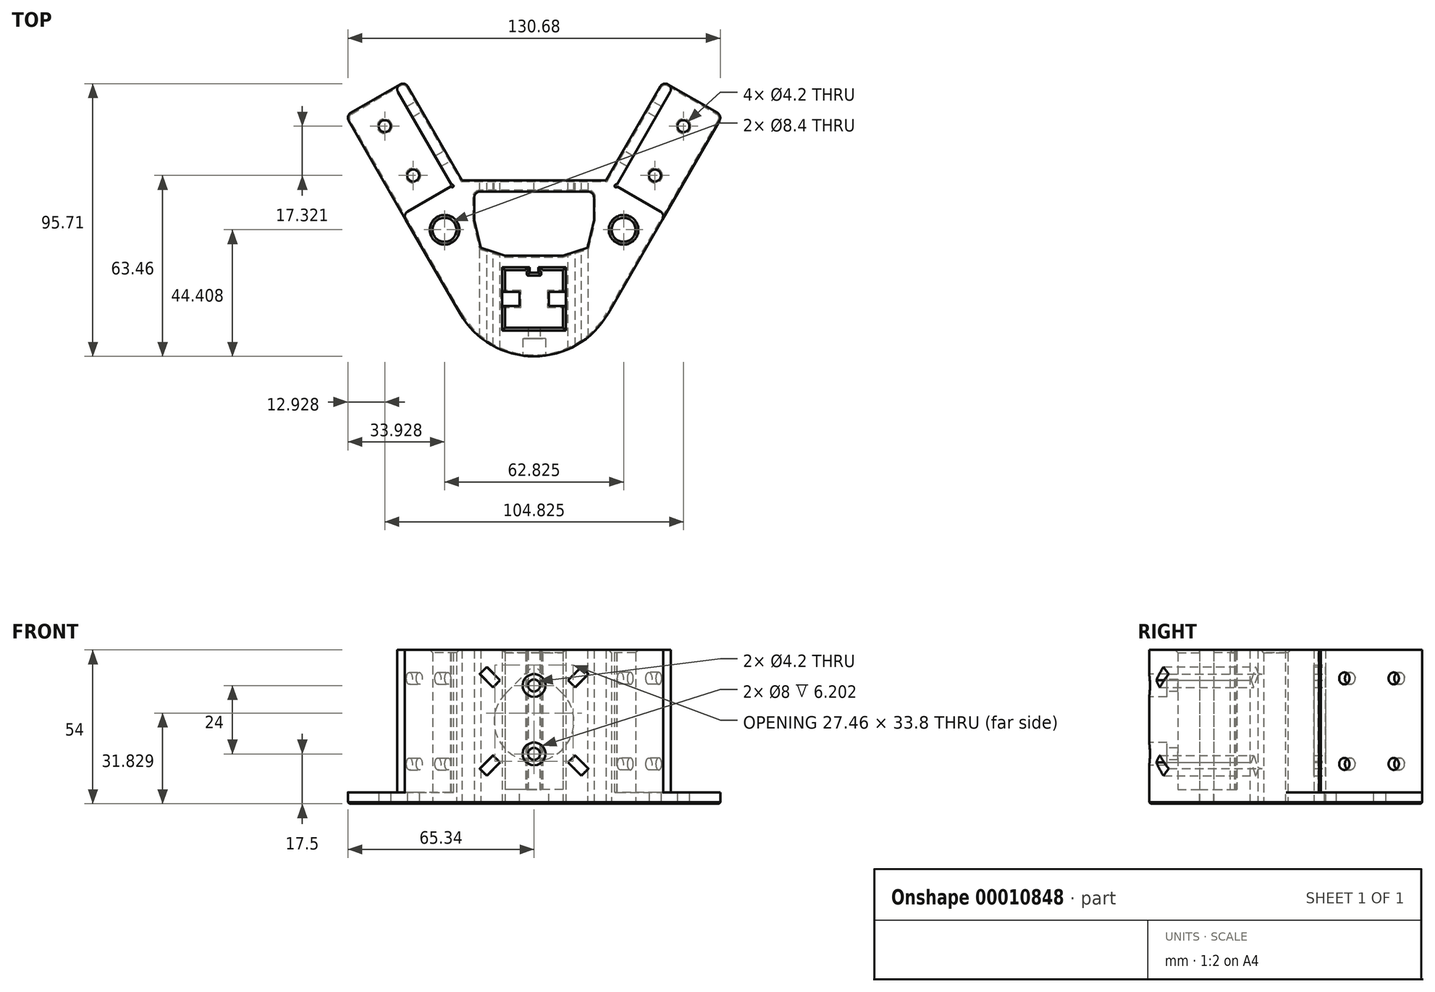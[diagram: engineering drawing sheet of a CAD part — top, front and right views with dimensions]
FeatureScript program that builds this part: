
annotation { "Feature Type Name" : "Feature", "Feature Type Description" : "" }
export const myFeature = defineFeature(function(context is Context, id is Id, definition is map)
    precondition{}
    {
        {
            var Q0;
            Q0=qCreatedBy(makeId("Top.planeOp"),FACE);
            var sketch = newSketch(context, id + "F0", { "sketchPlane" : qUnion([Q0])});
            skLineSegment(sketch, "E0.rect.bottom", {"start": v(10.15, -10.15) * mm, "end": v(-10.15, -10.15) * mm});
            skLineSegment(sketch, "E0.rect.top", {"start": v(10.15, 10.15) * mm, "end": v(-10.15, 10.15) * mm});
            skLineSegment(sketch, "E0.rect.left", {"start": v(10.15, -10.15) * mm, "end": v(10.15, 10.15) * mm});
            skLineSegment(sketch, "E0.rect.right", {"start": v(-10.15, -10.15) * mm, "end": v(-10.15, 10.15) * mm});
            skPoint(sketch, "E0.rect.middle", {"position": v(0, 0) * mm});
            skLineSegment(sketch, "E1", {"start": v(-10.15, -2.5) * mm, "end": v(-8.15, -2.5) * mm});
            skLineSegment(sketch, "E2", {"start": v(-8.15, -2.5) * mm, "end": v(-8.15, 2.5) * mm});
            skLineSegment(sketch, "E3", {"start": v(-8.15, 2.5) * mm, "end": v(-10.15, 2.5) * mm});
            skLineSegment(sketch, "E4", {"start": v(-2.5, 10.15) * mm, "end": v(-2.5, 8.15) * mm});
            skLineSegment(sketch, "E5", {"start": v(-2.5, 8.15) * mm, "end": v(2.5, 8.15) * mm});
            skLineSegment(sketch, "E6", {"start": v(2.5, 8.15) * mm, "end": v(2.5, 10.15) * mm});
            skLineSegment(sketch, "E7", {"start": v(10.15, 2.5) * mm, "end": v(8.15, 2.5) * mm});
            skLineSegment(sketch, "E8", {"start": v(8.15, 2.5) * mm, "end": v(8.15, -2.5) * mm});
            skLineSegment(sketch, "E9", {"start": v(8.15, -2.5) * mm, "end": v(10.15, -2.5) * mm});
            skLineSegment(sketch, "E10", {"start": v(-25.98, -5.15) * mm, "end": v(-66.07, 64.3) * mm});
            skLineSegment(sketch, "E11", {"start": v(-66.07, 64.3) * mm, "end": v(-45.29, 76.3) * mm});
            skLineSegment(sketch, "E12", {"start": v(-45.29, 76.3) * mm, "end": v(-25.29, 41.65) * mm});
            skLineSegment(sketch, "E13", {"start": v(-25.29, 41.65) * mm, "end": v(25.29, 41.65) * mm});
            skLineSegment(sketch, "E14", {"start": v(25.29, 41.65) * mm, "end": v(45.29, 76.3) * mm});
            skLineSegment(sketch, "E15", {"start": v(45.29, 76.3) * mm, "end": v(66.07, 64.3) * mm});
            skLineSegment(sketch, "E16", {"start": v(66.07, 64.3) * mm, "end": v(25.98, -5.15) * mm});
            skPoint(sketch, "E17.visualSharp", {"position": v(0, -50.15) * mm});
            skArc(sketch, "E17.filletArc", {"start": v(-25.98, -5.15) * mm, "mid": v(0, -20.15) * mm, "end": v(25.98, -5.15) * mm});
            skLineSegment(sketch, "E18", {"start": v(-48.75, 74.3) * mm, "end": v(-28.75, 39.65) * mm});
            skLineSegment(sketch, "E19", {"start": v(-28.75, 39.65) * mm, "end": v(-46.07, 29.65) * mm});
            skLineSegment(sketch, "E20", {"start": v(48.75, 74.3) * mm, "end": v(28.75, 39.65) * mm});
            skLineSegment(sketch, "E21", {"start": v(28.75, 39.65) * mm, "end": v(46.07, 29.65) * mm});
            skLineSegment(sketch, "E22", {"start": v(-28.75, 39.65) * mm, "end": v(-25.29, 41.65) * mm, "construction": true});
            skLineSegment(sketch, "E23", {"start": v(-57.41, 69.3) * mm, "end": v(-37.41, 34.65) * mm, "construction": true});
            skCircle(sketch, "E24", {"center": v(-52.41, 60.63) * mm, "radius": 2.1 * mm});
            skCircle(sketch, "E25", {"center": v(-42.41, 43.31) * mm, "radius": 2.1 * mm});
            skCircle(sketch, "E26", {"center": v(52.41, 60.63) * mm, "radius": 2.1 * mm});
            skCircle(sketch, "E27", {"center": v(42.41, 43.31) * mm, "radius": 2.1 * mm});
            skLineSegment(sketch, "E28", {"start": v(-21, 37.65) * mm, "end": v(21, 37.65) * mm});
            skLineSegment(sketch, "E29", {"start": v(21, 37.65) * mm, "end": v(21, 27.65) * mm});
            skLineSegment(sketch, "E30", {"start": v(10.15, 15.15) * mm, "end": v(-10.15, 15.15) * mm});
            skLineSegment(sketch, "E31", {"start": v(-21, 27.65) * mm, "end": v(-21, 37.65) * mm});
            skLineSegment(sketch, "E32", {"start": v(-21, 27.65) * mm, "end": v(-18.71, 17.91) * mm});
            skLineSegment(sketch, "E33", {"start": v(-18.71, 17.91) * mm, "end": v(-10.15, 15.15) * mm});
            skLineSegment(sketch, "E34", {"start": v(21, 27.65) * mm, "end": v(18.71, 17.91) * mm});
            skLineSegment(sketch, "E35", {"start": v(18.71, 17.91) * mm, "end": v(10.15, 15.15) * mm});
            skLineSegment(sketch, "E36", {"start": v(-37.41, 34.65) * mm, "end": v(-20.62, 5.56) * mm, "construction": true});
            skCircle(sketch, "E37", {"center": v(-31.41, 24.26) * mm, "radius": 4.2 * mm});
            skLineSegment(sketch, "E38", {"start": v(0, -71.13) * mm, "end": v(0, 233.1) * mm, "construction": true});
            skCircle(sketch, "E39", {"center": v(31.41, 24.26) * mm, "radius": 4.2 * mm});
            skSolve(sketch);
        }
        {
            var Q0;
            {var subQ5=sQuery(id+"F0.wireOp",EDGE,"E0.rect.bottom");Q0=makeQuery(id+"F0.imprint","IMPRINT",FACE,{"disambiguationData":[TD([[makeQuery(id+"F0.imprint","IMPRINT",EDGE,{"derivedFrom":subQ5}),1.0]])]});}
            var Q1;
            {var subQ1=sQuery(id+"F0.wireOp",EDGE,"E18");Q1=makeQuery(id+"F0.imprint","IMPRINT",FACE,{"disambiguationData":[TD([[makeQuery(id+"F0.imprint","IMPRINT",EDGE,{"derivedFrom":subQ1}),-1.0]])]});}
            var Q2;
            {var subQ0=sQuery(id+"F0.wireOp",EDGE,"E20");Q2=makeQuery(id+"F0.imprint","IMPRINT",FACE,{"disambiguationData":[TD([[makeQuery(id+"F0.imprint","IMPRINT",EDGE,{"derivedFrom":subQ0}),1.0]])]});}
            var Q3;
            {var subQ1=sQuery(id+"F0.wireOp",EDGE,"E1");Q3=makeQuery(id+"F0.imprint","IMPRINT",FACE,{"disambiguationData":[TD([[makeQuery(id+"F0.imprint","IMPRINT",EDGE,{"derivedFrom":subQ1}),1.0]])]});}
            var Q4;
            {var subQ1=sQuery(id+"F0.wireOp",EDGE,"E4");Q4=makeQuery(id+"F0.imprint","IMPRINT",FACE,{"disambiguationData":[TD([[makeQuery(id+"F0.imprint","IMPRINT",EDGE,{"derivedFrom":subQ1}),1.0]])]});}
            var Q5;
            {var subQ1=sQuery(id+"F0.wireOp",EDGE,"E7");Q5=makeQuery(id+"F0.imprint","IMPRINT",FACE,{"disambiguationData":[TD([[makeQuery(id+"F0.imprint","IMPRINT",EDGE,{"derivedFrom":subQ1}),1.0]])]});}
            extrude(context, id + "F1", {"entities" : qUnion([Q0, Q1, Q2, Q3, Q4, Q5]), "depth" : 4 * mm});
        }
        {
            var Q0;
            Q0=makeQuery(id+"F1.opExtrude","CAP_FACE",FACE,{"disambiguationData":[OSD([sQuery(id+"F0.wireOp",EDGE,"E0.rect.bottom"),sQuery(id+"F0.wireOp",EDGE,"E0.rect.top"),sQuery(id+"F0.wireOp",EDGE,"E0.rect.left"),sQuery(id+"F0.wireOp",EDGE,"E0.rect.right"),sQuery(id+"F0.wireOp",EDGE,"E1"),sQuery(id+"F0.wireOp",EDGE,"E2"),sQuery(id+"F0.wireOp",EDGE,"E3"),sQuery(id+"F0.wireOp",EDGE,"E4"),sQuery(id+"F0.wireOp",EDGE,"E5"),sQuery(id+"F0.wireOp",EDGE,"E6"),sQuery(id+"F0.wireOp",EDGE,"E7"),sQuery(id+"F0.wireOp",EDGE,"E8"),sQuery(id+"F0.wireOp",EDGE,"E9"),sQuery(id+"F0.wireOp",EDGE,"E10"),sQuery(id+"F0.wireOp",EDGE,"E11"),sQuery(id+"F0.wireOp",EDGE,"E12"),sQuery(id+"F0.wireOp",EDGE,"E13"),sQuery(id+"F0.wireOp",EDGE,"E14"),sQuery(id+"F0.wireOp",EDGE,"E15"),sQuery(id+"F0.wireOp",EDGE,"E16"),sQuery(id+"F0.wireOp",EDGE,"E17.filletArc"),sQuery(id+"F0.wireOp",EDGE,"E24"),sQuery(id+"F0.wireOp",EDGE,"E25"),sQuery(id+"F0.wireOp",EDGE,"E26"),sQuery(id+"F0.wireOp",EDGE,"E27"),sQuery(id+"F0.wireOp",EDGE,"E28"),sQuery(id+"F0.wireOp",EDGE,"E29"),sQuery(id+"F0.wireOp",EDGE,"E30"),sQuery(id+"F0.wireOp",EDGE,"E31"),sQuery(id+"F0.wireOp",EDGE,"E32"),sQuery(id+"F0.wireOp",EDGE,"E33"),sQuery(id+"F0.wireOp",EDGE,"E34"),sQuery(id+"F0.wireOp",EDGE,"E35"),sQuery(id+"F0.wireOp",EDGE,"E37"),sQuery(id+"F0.wireOp",EDGE,"E39")])],"isStart":false});
            var sketch = newSketch(context, id + "F2", { "sketchPlane" : qUnion([Q0])});
            skLineSegment(sketch, "E40.0", {"start": v(-48.75, 74.3) * mm, "end": v(-28.75, 39.65) * mm});
            skLineSegment(sketch, "E41.0", {"start": v(-28.75, 39.65) * mm, "end": v(-46.07, 29.65) * mm});
            skLineSegment(sketch, "E42.0", {"start": v(48.75, 74.3) * mm, "end": v(28.75, 39.65) * mm});
            skLineSegment(sketch, "E43.0", {"start": v(28.75, 39.65) * mm, "end": v(46.07, 29.65) * mm});
            skSolve(sketch);
        }
        {
            var Q0;
            {var subQ7=sQuery(id+"F2.wireOp",EDGE,"E40.0");Q0=makeQuery(id+"F2.imprint","IMPRINT",FACE,{"disambiguationData":[TD([[makeQuery(id+"F2.imprint","IMPRINT",EDGE,{"derivedFrom":subQ7}),1.0]])]});}
            extrude(context, id + "F3", {"entities" : qUnion([Q0]), "operationType" : NewBodyOperationType.ADD, "depth" : 50 * mm});
        }
        {
            var Q0;
            {var subQ0=sQuery(id+"F0.wireOp",EDGE,"E13");Q0=makeQuery(id+"F3.boolean.opBoolean","MERGE",FACE,{"derivedFrom":[makeQuery(id+"F1.opExtrude","SWEPT_FACE",FACE,{"disambiguationData":[OSD([subQ0])]}),makeQuery(id+"F3.opExtrude","SWEPT_FACE",FACE,{"disambiguationData":[OSD([subQ0])]})]});}
            var sketch = newSketch(context, id + "F4", { "sketchPlane" : qUnion([Q0])});
            skCircle(sketch, "E44", {"center": v(0, 28.93) * mm, "radius": 14 * mm});
            skLineSegment(sketch, "E45", {"start": v(0, 28.93) * mm, "end": v(-14.76, 43.7) * mm, "construction": true});
            skLineSegment(sketch, "E46", {"start": v(-19.07, 45.53) * mm, "end": v(-16.6, 48) * mm});
            skLineSegment(sketch, "E47", {"start": v(-16.6, 48) * mm, "end": v(-11.93, 43.33) * mm});
            skLineSegment(sketch, "E48", {"start": v(-11.93, 43.33) * mm, "end": v(-14.4, 40.86) * mm});
            skLineSegment(sketch, "E49", {"start": v(-14.4, 40.86) * mm, "end": v(-19.07, 45.53) * mm});
            skLineSegment(sketch, "E50.1.0", {"start": v(-11.93, 14.53) * mm, "end": v(-16.6, 9.86) * mm});
            skLineSegment(sketch, "E50.1.1", {"start": v(-16.6, 9.86) * mm, "end": v(-19.07, 12.33) * mm});
            skLineSegment(sketch, "E50.1.2", {"start": v(-19.07, 12.33) * mm, "end": v(-14.4, 17) * mm});
            skLineSegment(sketch, "E50.1.3", {"start": v(-14.4, 17) * mm, "end": v(-11.93, 14.53) * mm});
            skLineSegment(sketch, "E50.2.0", {"start": v(14.4, 17) * mm, "end": v(19.07, 12.33) * mm});
            skLineSegment(sketch, "E50.2.1", {"start": v(19.07, 12.33) * mm, "end": v(16.6, 9.86) * mm});
            skLineSegment(sketch, "E50.2.2", {"start": v(16.6, 9.86) * mm, "end": v(11.93, 14.53) * mm});
            skLineSegment(sketch, "E50.2.3", {"start": v(11.93, 14.53) * mm, "end": v(14.4, 17) * mm});
            skLineSegment(sketch, "E50.3.0", {"start": v(11.93, 43.33) * mm, "end": v(16.6, 48) * mm});
            skLineSegment(sketch, "E50.3.1", {"start": v(16.6, 48) * mm, "end": v(19.07, 45.53) * mm});
            skLineSegment(sketch, "E50.3.2", {"start": v(19.07, 45.53) * mm, "end": v(14.4, 40.86) * mm});
            skLineSegment(sketch, "E50.3.3", {"start": v(14.4, 40.86) * mm, "end": v(11.93, 43.33) * mm});
            skLineSegment(sketch, "E51", {"start": v(0, 48.73) * mm, "end": v(-9.9, 38.83) * mm});
            skLineSegment(sketch, "E52", {"start": v(0, 48.73) * mm, "end": v(9.9, 38.83) * mm});
            skSolve(sketch);
        }
        {
            var Q0;
            Q0=makeQuery(id+"F4.imprint","IMPRINT",FACE,{"disambiguationData":[TD([[makeQuery(id+"F4.imprint","IMPRINT",EDGE,{"derivedFrom":sQuery(id+"F4.wireOp",EDGE,"E44")}),1.0]])]});
            var Q1;
            {var subQ1=sQuery(id+"F4.wireOp",EDGE,"E51");Q1=makeQuery(id+"F4.imprint","IMPRINT",FACE,{"disambiguationData":[TD([[makeQuery(id+"F4.imprint","IMPRINT",EDGE,{"derivedFrom":subQ1}),1.0]])]});}
            extrude(context, id + "F5", {"entities" : qUnion([Q0, Q1]), "operationType" : NewBodyOperationType.REMOVE, "endBound" : BoundingType.UP_TO_NEXT, "oppositeDirection" : true, "depth" : 25 * mm});
        }
        {
            var Q0;
            Q0=makeQuery(id+"F4.imprint","IMPRINT",FACE,{"disambiguationData":[TD([[makeQuery(id+"F4.imprint","IMPRINT",EDGE,{"derivedFrom":sQuery(id+"F4.wireOp",EDGE,"E46")}),-1.0]])]});
            var Q1;
            Q1=makeQuery(id+"F4.imprint","IMPRINT",FACE,{"disambiguationData":[TD([[makeQuery(id+"F4.imprint","IMPRINT",EDGE,{"derivedFrom":sQuery(id+"F4.wireOp",EDGE,"E50.3.0")}),-1.0]])]});
            var Q2;
            Q2=makeQuery(id+"F4.imprint","IMPRINT",FACE,{"disambiguationData":[TD([[makeQuery(id+"F4.imprint","IMPRINT",EDGE,{"derivedFrom":sQuery(id+"F4.wireOp",EDGE,"E50.2.0")}),-1.0]])]});
            var Q3;
            Q3=makeQuery(id+"F4.imprint","IMPRINT",FACE,{"disambiguationData":[TD([[makeQuery(id+"F4.imprint","IMPRINT",EDGE,{"derivedFrom":sQuery(id+"F4.wireOp",EDGE,"E50.1.0")}),-1.0]])]});
            extrude(context, id + "F6", {"entities" : qUnion([Q0, Q1, Q2, Q3]), "operationType" : NewBodyOperationType.REMOVE, "endBound" : BoundingType.THROUGH_ALL, "oppositeDirection" : true, "depth" : 25 * mm});
        }
        {
            var Q0;
            {var subQ11=sQuery(id+"F0.wireOp",EDGE,"E0.rect.bottom");Q0=makeQuery(id+"F0.imprint","IMPRINT",FACE,{"disambiguationData":[TD([[makeQuery(id+"F0.imprint","IMPRINT",EDGE,{"derivedFrom":subQ11}),-1.0]])]});}
            extrude(context, id + "F7", {"entities" : qUnion([Q0]), "operationType" : NewBodyOperationType.ADD, "depth" : 5 * mm});
        }
        {
            var Q0;
            {var subQ0=sQuery(id+"F0.wireOp",EDGE,"E28");Q0=makeQuery(id+"F3.boolean.opBoolean","MERGE",FACE,{"derivedFrom":[makeQuery(id+"F1.opExtrude","SWEPT_FACE",FACE,{"disambiguationData":[OSD([subQ0])]}),makeQuery(id+"F3.opExtrude","SWEPT_FACE",FACE,{"disambiguationData":[OSD([subQ0])]})]});}
            cPlane(context, id + "F8", {"entities" : qUnion([Q0]), "cplaneType" : CPlaneType.OFFSET, "offset" : 100 * mm, "width" : 150 * mm, "height" : 150 * mm});
        }
        {
            var Q0;
            Q0=qCreatedBy(id+"F8.planeOp",FACE);
            var sketch = newSketch(context, id + "F9", { "sketchPlane" : qUnion([Q0])});
            skCircle(sketch, "E53", {"center": v(0, 41.5) * mm, "radius": 2.1 * mm});
            skCircle(sketch, "E54", {"center": v(0, 41.5) * mm, "radius": 4 * mm});
            skCircle(sketch, "E55", {"center": v(0, 17.5) * mm, "radius": 2.1 * mm});
            skCircle(sketch, "E56", {"center": v(0, 17.5) * mm, "radius": 4 * mm});
            skSolve(sketch);
        }
        {
            var Q0;
            Q0=makeQuery(id+"F9.imprint","IMPRINT",FACE,{"disambiguationData":[TD([[makeQuery(id+"F9.imprint","IMPRINT",EDGE,{"derivedFrom":sQuery(id+"F9.wireOp",EDGE,"E53")}),1.0]])]});
            var Q1;
            Q1=makeQuery(id+"F9.imprint","IMPRINT",FACE,{"disambiguationData":[TD([[makeQuery(id+"F9.imprint","IMPRINT",EDGE,{"derivedFrom":sQuery(id+"F9.wireOp",EDGE,"E55")}),1.0]])]});
            var Q2;
            {var subQ0=sQuery(id+"F0.wireOp",EDGE,"E0.rect.bottom");Q2=makeQuery(id+"F3.boolean.opBoolean","MERGE",FACE,{"derivedFrom":[makeQuery(id+"F1.opExtrude","SWEPT_FACE",FACE,{"disambiguationData":[OSD([subQ0])]}),makeQuery(id+"F3.opExtrude","SWEPT_FACE",FACE,{"disambiguationData":[OSD([subQ0])]})]});}
            extrude(context, id + "F10", {"entities" : qUnion([Q0, Q1]), "operationType" : NewBodyOperationType.REMOVE, "endBound" : BoundingType.UP_TO_SURFACE, "oppositeDirection" : true, "endBoundEntityFace" : qUnion([Q2]), "depth" : 25 * mm});
        }
        {
            var Q0;
            Q0=makeQuery(id+"F9.imprint","IMPRINT",FACE,{"disambiguationData":[TD([[makeQuery(id+"F9.imprint","IMPRINT",EDGE,{"derivedFrom":sQuery(id+"F9.wireOp",EDGE,"E53")}),-1.0]])]});
            var Q1;
            Q1=makeQuery(id+"F9.imprint","IMPRINT",FACE,{"disambiguationData":[TD([[makeQuery(id+"F9.imprint","IMPRINT",EDGE,{"derivedFrom":sQuery(id+"F9.wireOp",EDGE,"E55")}),-1.0]])]});
            extrude(context, id + "F11", {"entities" : qUnion([Q0, Q1]), "operationType" : NewBodyOperationType.REMOVE, "oppositeDirection" : true, "depth" : 48.4 * mm});
        }
        {
            var Q0;
            {var subQ0=sQuery(id+"F0.wireOp",EDGE,"E12");Q0=makeQuery(id+"F3.boolean.opBoolean","MERGE",FACE,{"derivedFrom":[makeQuery(id+"F1.opExtrude","SWEPT_FACE",FACE,{"disambiguationData":[OSD([subQ0])]}),makeQuery(id+"F3.opExtrude","SWEPT_FACE",FACE,{"disambiguationData":[OSD([subQ0])]})]});}
            var sketch = newSketch(context, id + "F12", { "sketchPlane" : qUnion([Q0])});
            skCircle(sketch, "E57", {"center": v(78.71, 44) * mm, "radius": 2.1 * mm});
            skCircle(sketch, "E58", {"center": v(58.71, 44) * mm, "radius": 2.1 * mm});
            skCircle(sketch, "E59", {"center": v(78.71, 14) * mm, "radius": 2.1 * mm});
            skCircle(sketch, "E60", {"center": v(58.71, 14) * mm, "radius": 2.1 * mm});
            skSolve(sketch);
        }
        {
            var Q0;
            Q0 = qSketchRegion(id + "F12", true);
            extrude(context, id + "F13", {"entities" : qUnion([Q0]), "operationType" : NewBodyOperationType.REMOVE, "oppositeDirection" : true, "depth" : 25 * mm});
        }
        {
            var Q0;
            {var subQ0=sQuery(id+"F0.wireOp",EDGE,"E14");Q0=makeQuery(id+"F3.boolean.opBoolean","MERGE",FACE,{"derivedFrom":[makeQuery(id+"F1.opExtrude","SWEPT_FACE",FACE,{"disambiguationData":[OSD([subQ0])]}),makeQuery(id+"F3.opExtrude","SWEPT_FACE",FACE,{"disambiguationData":[OSD([subQ0])]})]});}
            var sketch = newSketch(context, id + "F14", { "sketchPlane" : qUnion([Q0])});
            skCircle(sketch, "E61", {"center": v(-78.71, 44) * mm, "radius": 2.1 * mm});
            skCircle(sketch, "E62", {"center": v(-58.71, 44) * mm, "radius": 2.1 * mm});
            skCircle(sketch, "E63", {"center": v(-78.71, 14) * mm, "radius": 2.1 * mm});
            skCircle(sketch, "E64", {"center": v(-58.71, 14) * mm, "radius": 2.1 * mm});
            skSolve(sketch);
        }
        {
            var Q0;
            Q0 = qSketchRegion(id + "F14", true);
            extrude(context, id + "F15", {"entities" : qUnion([Q0]), "operationType" : NewBodyOperationType.REMOVE, "oppositeDirection" : true, "depth" : 25 * mm});
        }
        {
            var Q0;
            Q0=makeQuery(id+"F3.opExtrude","CAP_EDGE",EDGE,{"disambiguationData":[OSD([sQuery(id+"F0.wireOp",EDGE,"E0.rect.bottom")])],"isStart":false});
            var Q1;
            {var subQ0=sQuery(id+"F0.wireOp",EDGE,"E0.rect.left");Q1=makeQuery(id+"F3.opExtrude","CAP_EDGE",EDGE,{"disambiguationData":[OSD([subQ0]),TDD([makeQuery(id+"F2.imprint","IMPRINT",EDGE,{"derivedFrom":makeQuery(id+"F1.opExtrude","CAP_EDGE",EDGE,{"disambiguationData":[OSD([subQ0]),TDD([makeQuery(id+"F0.imprint","IMPRINT",EDGE,{"disambiguationData":[TD([[makeQuery(id+"F0.imprint","INTERSECT",VERTEX,{"derivedFrom":[sQuery(id+"F0.wireOp",EDGE,"E0.rect.bottom"),subQ0]}),-1.0]])],"derivedFrom":subQ0})])],"isStart":false})})])],"isStart":false});}
            var Q2;
            Q2=makeQuery(id+"F3.opExtrude","CAP_EDGE",EDGE,{"disambiguationData":[OSD([sQuery(id+"F0.wireOp",EDGE,"E9")])],"isStart":false});
            var Q3;
            Q3=makeQuery(id+"F3.opExtrude","CAP_EDGE",EDGE,{"disambiguationData":[OSD([sQuery(id+"F0.wireOp",EDGE,"E8")])],"isStart":false});
            var Q4;
            Q4=makeQuery(id+"F3.opExtrude","CAP_EDGE",EDGE,{"disambiguationData":[OSD([sQuery(id+"F0.wireOp",EDGE,"E7")])],"isStart":false});
            var Q5;
            {var subQ0=sQuery(id+"F0.wireOp",EDGE,"E0.rect.left");Q5=makeQuery(id+"F3.opExtrude","CAP_EDGE",EDGE,{"disambiguationData":[OSD([subQ0]),TDD([makeQuery(id+"F2.imprint","IMPRINT",EDGE,{"derivedFrom":makeQuery(id+"F1.opExtrude","CAP_EDGE",EDGE,{"disambiguationData":[OSD([subQ0]),TDD([makeQuery(id+"F0.imprint","IMPRINT",EDGE,{"disambiguationData":[TD([[makeQuery(id+"F0.imprint","INTERSECT",VERTEX,{"derivedFrom":[sQuery(id+"F0.wireOp",EDGE,"E0.rect.top"),subQ0]}),1.0]])],"derivedFrom":subQ0})])],"isStart":false})})])],"isStart":false});}
            var Q6;
            {var subQ0=sQuery(id+"F0.wireOp",EDGE,"E0.rect.top");Q6=makeQuery(id+"F3.opExtrude","CAP_EDGE",EDGE,{"disambiguationData":[OSD([subQ0]),TDD([makeQuery(id+"F2.imprint","IMPRINT",EDGE,{"derivedFrom":makeQuery(id+"F1.opExtrude","CAP_EDGE",EDGE,{"disambiguationData":[OSD([subQ0]),TDD([makeQuery(id+"F0.imprint","IMPRINT",EDGE,{"disambiguationData":[TD([[makeQuery(id+"F0.imprint","INTERSECT",VERTEX,{"derivedFrom":[subQ0,sQuery(id+"F0.wireOp",EDGE,"E0.rect.left")]}),-1.0]])],"derivedFrom":subQ0})])],"isStart":false})})])],"isStart":false});}
            var Q7;
            Q7=makeQuery(id+"F3.opExtrude","CAP_EDGE",EDGE,{"disambiguationData":[OSD([sQuery(id+"F0.wireOp",EDGE,"E6")])],"isStart":false});
            var Q8;
            Q8=makeQuery(id+"F3.opExtrude","CAP_EDGE",EDGE,{"disambiguationData":[OSD([sQuery(id+"F0.wireOp",EDGE,"E5")])],"isStart":false});
            var Q9;
            Q9=makeQuery(id+"F3.opExtrude","CAP_EDGE",EDGE,{"disambiguationData":[OSD([sQuery(id+"F0.wireOp",EDGE,"E4")])],"isStart":false});
            var Q10;
            {var subQ0=sQuery(id+"F0.wireOp",EDGE,"E0.rect.top");Q10=makeQuery(id+"F3.opExtrude","CAP_EDGE",EDGE,{"disambiguationData":[OSD([subQ0]),TDD([makeQuery(id+"F2.imprint","IMPRINT",EDGE,{"derivedFrom":makeQuery(id+"F1.opExtrude","CAP_EDGE",EDGE,{"disambiguationData":[OSD([subQ0]),TDD([makeQuery(id+"F0.imprint","IMPRINT",EDGE,{"disambiguationData":[TD([[makeQuery(id+"F0.imprint","INTERSECT",VERTEX,{"derivedFrom":[subQ0,sQuery(id+"F0.wireOp",EDGE,"E0.rect.right")]}),1.0]])],"derivedFrom":subQ0})])],"isStart":false})})])],"isStart":false});}
            var Q11;
            {var subQ0=sQuery(id+"F0.wireOp",EDGE,"E0.rect.right");Q11=makeQuery(id+"F3.opExtrude","CAP_EDGE",EDGE,{"disambiguationData":[OSD([subQ0]),TDD([makeQuery(id+"F2.imprint","IMPRINT",EDGE,{"derivedFrom":makeQuery(id+"F1.opExtrude","CAP_EDGE",EDGE,{"disambiguationData":[OSD([subQ0]),TDD([makeQuery(id+"F0.imprint","IMPRINT",EDGE,{"disambiguationData":[TD([[makeQuery(id+"F0.imprint","INTERSECT",VERTEX,{"derivedFrom":[sQuery(id+"F0.wireOp",EDGE,"E0.rect.top"),subQ0]}),1.0]])],"derivedFrom":subQ0})])],"isStart":false})})])],"isStart":false});}
            var Q12;
            Q12=makeQuery(id+"F3.opExtrude","CAP_EDGE",EDGE,{"disambiguationData":[OSD([sQuery(id+"F0.wireOp",EDGE,"E3")])],"isStart":false});
            var Q13;
            Q13=makeQuery(id+"F3.opExtrude","CAP_EDGE",EDGE,{"disambiguationData":[OSD([sQuery(id+"F0.wireOp",EDGE,"E2")])],"isStart":false});
            var Q14;
            Q14=makeQuery(id+"F3.opExtrude","CAP_EDGE",EDGE,{"disambiguationData":[OSD([sQuery(id+"F0.wireOp",EDGE,"E1")])],"isStart":false});
            var Q15;
            {var subQ0=sQuery(id+"F0.wireOp",EDGE,"E0.rect.right");Q15=makeQuery(id+"F3.opExtrude","CAP_EDGE",EDGE,{"disambiguationData":[OSD([subQ0]),TDD([makeQuery(id+"F2.imprint","IMPRINT",EDGE,{"derivedFrom":makeQuery(id+"F1.opExtrude","CAP_EDGE",EDGE,{"disambiguationData":[OSD([subQ0]),TDD([makeQuery(id+"F0.imprint","IMPRINT",EDGE,{"disambiguationData":[TD([[makeQuery(id+"F0.imprint","INTERSECT",VERTEX,{"derivedFrom":[sQuery(id+"F0.wireOp",EDGE,"E0.rect.bottom"),subQ0]}),-1.0]])],"derivedFrom":subQ0})])],"isStart":false})})])],"isStart":false});}
            var Q16;
            Q16=makeQuery(id+"F3.opExtrude","CAP_EDGE",EDGE,{"disambiguationData":[OSD([sQuery(id+"F0.wireOp",EDGE,"E39")])],"isStart":false});
            var Q17;
            Q17=makeQuery(id+"F3.opExtrude","CAP_EDGE",EDGE,{"disambiguationData":[OSD([sQuery(id+"F0.wireOp",EDGE,"E37")])],"isStart":false});
            chamfer(context, id + "F16", {"entities" : qUnion([Q0, Q1, Q2, Q3, Q4, Q5, Q6, Q7, Q8, Q9, Q10, Q11, Q12, Q13, Q14, Q15, Q16, Q17]), "width" : 1 * mm, "tangentPropagation" : true});
        }
        {
            var Q0;
            Q0=makeQuery(id+"F3.opExtrude","CAP_FACE",FACE,{"disambiguationData":[OSD([sQuery(id+"F0.wireOp",EDGE,"E0.rect.bottom"),sQuery(id+"F0.wireOp",EDGE,"E0.rect.top"),sQuery(id+"F0.wireOp",EDGE,"E0.rect.left"),sQuery(id+"F0.wireOp",EDGE,"E0.rect.right"),sQuery(id+"F0.wireOp",EDGE,"E1"),sQuery(id+"F0.wireOp",EDGE,"E2"),sQuery(id+"F0.wireOp",EDGE,"E3"),sQuery(id+"F0.wireOp",EDGE,"E4"),sQuery(id+"F0.wireOp",EDGE,"E5"),sQuery(id+"F0.wireOp",EDGE,"E6"),sQuery(id+"F0.wireOp",EDGE,"E7"),sQuery(id+"F0.wireOp",EDGE,"E8"),sQuery(id+"F0.wireOp",EDGE,"E9"),sQuery(id+"F0.wireOp",EDGE,"E10"),sQuery(id+"F0.wireOp",EDGE,"E11"),sQuery(id+"F0.wireOp",EDGE,"E12"),sQuery(id+"F0.wireOp",EDGE,"E13"),sQuery(id+"F0.wireOp",EDGE,"E14"),sQuery(id+"F0.wireOp",EDGE,"E15"),sQuery(id+"F0.wireOp",EDGE,"E16"),sQuery(id+"F0.wireOp",EDGE,"E17.filletArc"),sQuery(id+"F0.wireOp",EDGE,"E28"),sQuery(id+"F0.wireOp",EDGE,"E29"),sQuery(id+"F0.wireOp",EDGE,"E30"),sQuery(id+"F0.wireOp",EDGE,"E31"),sQuery(id+"F0.wireOp",EDGE,"E32"),sQuery(id+"F0.wireOp",EDGE,"E33"),sQuery(id+"F0.wireOp",EDGE,"E34"),sQuery(id+"F0.wireOp",EDGE,"E35"),sQuery(id+"F0.wireOp",EDGE,"E37"),sQuery(id+"F0.wireOp",EDGE,"E39"),sQuery(id+"F2.wireOp",EDGE,"E40.0"),sQuery(id+"F2.wireOp",EDGE,"E41.0"),sQuery(id+"F2.wireOp",EDGE,"E42.0"),sQuery(id+"F2.wireOp",EDGE,"E43.0")])],"isStart":false});
            var sketch = newSketch(context, id + "F17", { "sketchPlane" : qUnion([Q0])});
            skCircle(sketch, "E65", {"center": v(-28.75, 39.65) * mm, "radius": 0.5 * mm});
            skCircle(sketch, "E66", {"center": v(28.75, 39.65) * mm, "radius": 0.5 * mm});
            skSolve(sketch);
        }
        {
            var Q0;
            {var subQ1=sQuery(id+"F17.wireOp",EDGE,"E65");var subQ3=makeQuery(id+"F3.opExtrude","CAP_EDGE",EDGE,{"disambiguationData":[OSD([sQuery(id+"F2.wireOp",EDGE,"E40.0")])],"isStart":false});var subQ5=makeQuery(id+"F17.imprint","INTERSECT",VERTEX,{"derivedFrom":[subQ3,subQ1]});Q0=makeQuery(id+"F17.imprint","IMPRINT",FACE,{"disambiguationData":[TD([[makeQuery(id+"F17.imprint","IMPRINT",EDGE,{"disambiguationData":[TD([[subQ5,1.0]])],"derivedFrom":subQ1}),1.0]])]});}
            var Q1;
            {var subQ1=sQuery(id+"F17.wireOp",EDGE,"E66");var subQ3=makeQuery(id+"F3.opExtrude","CAP_EDGE",EDGE,{"disambiguationData":[OSD([sQuery(id+"F2.wireOp",EDGE,"E42.0")])],"isStart":false});var subQ5=makeQuery(id+"F17.imprint","INTERSECT",VERTEX,{"derivedFrom":[subQ3,subQ1]});Q1=makeQuery(id+"F17.imprint","IMPRINT",FACE,{"disambiguationData":[TD([[makeQuery(id+"F17.imprint","IMPRINT",EDGE,{"disambiguationData":[TD([[subQ5,-1.0]])],"derivedFrom":subQ1}),1.0]])]});}
            var Q2;
            {var subQ0=sQuery(id+"F0.wireOp",EDGE,"E10");var subQ1=sQuery(id+"F0.wireOp",EDGE,"E11");var subQ2=sQuery(id+"F0.wireOp",EDGE,"E24");var subQ3=sQuery(id+"F0.wireOp",EDGE,"E25");Q2=makeQuery(id+"F3.boolean.opBoolean","SPLIT",FACE,{"disambiguationData":[TD([makeQuery(id+"F1.opExtrude","SWEPT_FACE",FACE,{"disambiguationData":[OSD([subQ0])]})])],"derivedFrom":makeQuery(id+"F1.opExtrude","CAP_FACE",FACE,{"disambiguationData":[OSD([sQuery(id+"F0.wireOp",EDGE,"E0.rect.bottom"),sQuery(id+"F0.wireOp",EDGE,"E0.rect.top"),sQuery(id+"F0.wireOp",EDGE,"E0.rect.left"),sQuery(id+"F0.wireOp",EDGE,"E0.rect.right"),sQuery(id+"F0.wireOp",EDGE,"E1"),sQuery(id+"F0.wireOp",EDGE,"E2"),sQuery(id+"F0.wireOp",EDGE,"E3"),sQuery(id+"F0.wireOp",EDGE,"E4"),sQuery(id+"F0.wireOp",EDGE,"E5"),sQuery(id+"F0.wireOp",EDGE,"E6"),sQuery(id+"F0.wireOp",EDGE,"E7"),sQuery(id+"F0.wireOp",EDGE,"E8"),sQuery(id+"F0.wireOp",EDGE,"E9"),subQ0,subQ1,sQuery(id+"F0.wireOp",EDGE,"E12"),sQuery(id+"F0.wireOp",EDGE,"E13"),sQuery(id+"F0.wireOp",EDGE,"E14"),sQuery(id+"F0.wireOp",EDGE,"E15"),sQuery(id+"F0.wireOp",EDGE,"E16"),sQuery(id+"F0.wireOp",EDGE,"E17.filletArc"),subQ2,subQ3,sQuery(id+"F0.wireOp",EDGE,"E26"),sQuery(id+"F0.wireOp",EDGE,"E27"),sQuery(id+"F0.wireOp",EDGE,"E28"),sQuery(id+"F0.wireOp",EDGE,"E29"),sQuery(id+"F0.wireOp",EDGE,"E30"),sQuery(id+"F0.wireOp",EDGE,"E31"),sQuery(id+"F0.wireOp",EDGE,"E32"),sQuery(id+"F0.wireOp",EDGE,"E33"),sQuery(id+"F0.wireOp",EDGE,"E34"),sQuery(id+"F0.wireOp",EDGE,"E35"),sQuery(id+"F0.wireOp",EDGE,"E37"),sQuery(id+"F0.wireOp",EDGE,"E39")])],"isStart":false})});}
            extrude(context, id + "F18", {"entities" : qUnion([Q0, Q1]), "operationType" : NewBodyOperationType.REMOVE, "endBound" : BoundingType.UP_TO_SURFACE, "oppositeDirection" : true, "endBoundEntityFace" : qUnion([Q2]), "depth" : 25 * mm});
        }
        {
            var Q0;
            Q0=makeQuery(id+"F18.boolean.opBoolean","COPY",EDGE,{"derivedFrom":makeQuery(id+"F18.opExtrude","SWEPT_EDGE",EDGE,{"disambiguationData":[OSD([sQuery(id+"F2.wireOp",EDGE,"E40.0"),sQuery(id+"F17.wireOp",EDGE,"E65")])]})});
            var Q1;
            Q1=makeQuery(id+"F18.boolean.opBoolean","COPY",EDGE,{"derivedFrom":makeQuery(id+"F18.opExtrude","SWEPT_EDGE",EDGE,{"disambiguationData":[OSD([sQuery(id+"F2.wireOp",EDGE,"E41.0"),sQuery(id+"F17.wireOp",EDGE,"E65")])]})});
            var Q2;
            Q2=makeQuery(id+"F18.boolean.opBoolean","COPY",EDGE,{"derivedFrom":makeQuery(id+"F18.opExtrude","SWEPT_EDGE",EDGE,{"disambiguationData":[OSD([sQuery(id+"F2.wireOp",EDGE,"E42.0"),sQuery(id+"F17.wireOp",EDGE,"E66")])]})});
            var Q3;
            Q3=makeQuery(id+"F18.boolean.opBoolean","COPY",EDGE,{"derivedFrom":makeQuery(id+"F18.opExtrude","SWEPT_EDGE",EDGE,{"disambiguationData":[OSD([sQuery(id+"F2.wireOp",EDGE,"E43.0"),sQuery(id+"F17.wireOp",EDGE,"E66")])]})});
            var Q4;
            Q4=makeQuery(id+"F3.opExtrude","SWEPT_EDGE",EDGE,{"disambiguationData":[OSD([sQuery(id+"F0.wireOp",EDGE,"E10"),sQuery(id+"F2.wireOp",EDGE,"E41.0")])]});
            var Q5;
            Q5=makeQuery(id+"F1.opExtrude","SWEPT_EDGE",EDGE,{"disambiguationData":[OSD([sQuery(id+"F0.wireOp",EDGE,"E10"),sQuery(id+"F0.wireOp",EDGE,"E11")])]});
            var Q6;
            Q6=makeQuery(id+"F3.opExtrude","SWEPT_EDGE",EDGE,{"disambiguationData":[OSD([sQuery(id+"F0.wireOp",EDGE,"E11"),sQuery(id+"F2.wireOp",EDGE,"E40.0")])]});
            var Q7;
            {var subQ0=sQuery(id+"F0.wireOp",EDGE,"E11");var subQ1=sQuery(id+"F0.wireOp",EDGE,"E12");Q7=makeQuery(id+"F3.boolean.opBoolean","MERGE",EDGE,{"derivedFrom":[makeQuery(id+"F1.opExtrude","SWEPT_EDGE",EDGE,{"disambiguationData":[OSD([subQ0,subQ1])]}),makeQuery(id+"F3.opExtrude","SWEPT_EDGE",EDGE,{"disambiguationData":[OSD([subQ0,subQ1])]})]});}
            var Q8;
            {var subQ0=sQuery(id+"F0.wireOp",EDGE,"E14");var subQ1=sQuery(id+"F0.wireOp",EDGE,"E15");Q8=makeQuery(id+"F3.boolean.opBoolean","MERGE",EDGE,{"derivedFrom":[makeQuery(id+"F1.opExtrude","SWEPT_EDGE",EDGE,{"disambiguationData":[OSD([subQ0,subQ1])]}),makeQuery(id+"F3.opExtrude","SWEPT_EDGE",EDGE,{"disambiguationData":[OSD([subQ0,subQ1])]})]});}
            var Q9;
            Q9=makeQuery(id+"F3.opExtrude","SWEPT_EDGE",EDGE,{"disambiguationData":[OSD([sQuery(id+"F0.wireOp",EDGE,"E15"),sQuery(id+"F2.wireOp",EDGE,"E42.0")])]});
            var Q10;
            Q10=makeQuery(id+"F1.opExtrude","SWEPT_EDGE",EDGE,{"disambiguationData":[OSD([sQuery(id+"F0.wireOp",EDGE,"E15"),sQuery(id+"F0.wireOp",EDGE,"E16")])]});
            var Q11;
            Q11=makeQuery(id+"F3.opExtrude","SWEPT_EDGE",EDGE,{"disambiguationData":[OSD([sQuery(id+"F0.wireOp",EDGE,"E16"),sQuery(id+"F2.wireOp",EDGE,"E43.0")])]});
            var Q12;
            {var subQ0=sQuery(id+"F0.wireOp",EDGE,"E28");var subQ1=sQuery(id+"F0.wireOp",EDGE,"E31");Q12=makeQuery(id+"F3.boolean.opBoolean","MERGE",EDGE,{"derivedFrom":[makeQuery(id+"F1.opExtrude","SWEPT_EDGE",EDGE,{"disambiguationData":[OSD([subQ0,subQ1])]}),makeQuery(id+"F3.opExtrude","SWEPT_EDGE",EDGE,{"disambiguationData":[OSD([subQ0,subQ1])]})]});}
            var Q13;
            {var subQ0=sQuery(id+"F0.wireOp",EDGE,"E28");var subQ1=sQuery(id+"F0.wireOp",EDGE,"E29");Q13=makeQuery(id+"F3.boolean.opBoolean","MERGE",EDGE,{"derivedFrom":[makeQuery(id+"F1.opExtrude","SWEPT_EDGE",EDGE,{"disambiguationData":[OSD([subQ0,subQ1])]}),makeQuery(id+"F3.opExtrude","SWEPT_EDGE",EDGE,{"disambiguationData":[OSD([subQ0,subQ1])]})]});}
            fillet(context, id + "F19", {"entities" : qUnion([Q0, Q1, Q2, Q3, Q4, Q5, Q6, Q7, Q8, Q9, Q10, Q11, Q12, Q13]), "radius" : 2 * mm, "tangentPropagation" : true, "allowEdgeOverflow" : false});
        }
        {
            var Q0;
            {var subQ0=sQuery(id+"F0.wireOp",EDGE,"E0.rect.bottom");var subQ1=sQuery(id+"F0.wireOp",EDGE,"E0.rect.top");var subQ2=sQuery(id+"F0.wireOp",EDGE,"E0.rect.left");var subQ3=sQuery(id+"F0.wireOp",EDGE,"E0.rect.right");var subQ4=sQuery(id+"F0.wireOp",EDGE,"E1");var subQ5=sQuery(id+"F0.wireOp",EDGE,"E2");var subQ6=sQuery(id+"F0.wireOp",EDGE,"E3");var subQ7=sQuery(id+"F0.wireOp",EDGE,"E4");var subQ8=sQuery(id+"F0.wireOp",EDGE,"E5");var subQ9=sQuery(id+"F0.wireOp",EDGE,"E6");var subQ10=sQuery(id+"F0.wireOp",EDGE,"E7");var subQ11=sQuery(id+"F0.wireOp",EDGE,"E8");var subQ12=sQuery(id+"F0.wireOp",EDGE,"E9");Q0=makeQuery(id+"F7.boolean.opBoolean","MERGE",FACE,{"derivedFrom":[makeQuery(id+"F1.opExtrude","CAP_FACE",FACE,{"disambiguationData":[OSD([subQ0,subQ1,subQ2,subQ3,subQ4,subQ5,subQ6,subQ7,subQ8,subQ9,subQ10,subQ11,subQ12,sQuery(id+"F0.wireOp",EDGE,"E10"),sQuery(id+"F0.wireOp",EDGE,"E11"),sQuery(id+"F0.wireOp",EDGE,"E12"),sQuery(id+"F0.wireOp",EDGE,"E13"),sQuery(id+"F0.wireOp",EDGE,"E14"),sQuery(id+"F0.wireOp",EDGE,"E15"),sQuery(id+"F0.wireOp",EDGE,"E16"),sQuery(id+"F0.wireOp",EDGE,"E17.filletArc"),sQuery(id+"F0.wireOp",EDGE,"E24"),sQuery(id+"F0.wireOp",EDGE,"E25"),sQuery(id+"F0.wireOp",EDGE,"E26"),sQuery(id+"F0.wireOp",EDGE,"E27"),sQuery(id+"F0.wireOp",EDGE,"E28"),sQuery(id+"F0.wireOp",EDGE,"E29"),sQuery(id+"F0.wireOp",EDGE,"E30"),sQuery(id+"F0.wireOp",EDGE,"E31"),sQuery(id+"F0.wireOp",EDGE,"E32"),sQuery(id+"F0.wireOp",EDGE,"E33"),sQuery(id+"F0.wireOp",EDGE,"E34"),sQuery(id+"F0.wireOp",EDGE,"E35"),sQuery(id+"F0.wireOp",EDGE,"E37"),sQuery(id+"F0.wireOp",EDGE,"E39")])],"isStart":true}),makeQuery(id+"F7.opExtrude","CAP_FACE",FACE,{"disambiguationData":[OSD([subQ0,subQ1,subQ2,subQ3,subQ4,subQ5,subQ6,subQ7,subQ8,subQ9,subQ10,subQ11,subQ12])],"isStart":true})]});}
            chamfer(context, id + "F20", {"entities" : qUnion([Q0]), "width" : 0.5 * mm, "tangentPropagation" : true});
        }
        {
            var Q0;
            Q0=makeQuery(id+"F7.opExtrude","CAP_FACE",FACE,{"disambiguationData":[OSD([sQuery(id+"F0.wireOp",EDGE,"E0.rect.bottom"),sQuery(id+"F0.wireOp",EDGE,"E0.rect.top"),sQuery(id+"F0.wireOp",EDGE,"E0.rect.left"),sQuery(id+"F0.wireOp",EDGE,"E0.rect.right"),sQuery(id+"F0.wireOp",EDGE,"E1"),sQuery(id+"F0.wireOp",EDGE,"E2"),sQuery(id+"F0.wireOp",EDGE,"E3"),sQuery(id+"F0.wireOp",EDGE,"E4"),sQuery(id+"F0.wireOp",EDGE,"E5"),sQuery(id+"F0.wireOp",EDGE,"E6"),sQuery(id+"F0.wireOp",EDGE,"E7"),sQuery(id+"F0.wireOp",EDGE,"E8"),sQuery(id+"F0.wireOp",EDGE,"E9")])],"isStart":false});
            var sketch = newSketch(context, id + "F21", { "sketchPlane" : qUnion([Q0])});
            skCircle(sketch, "E67", {"center": v(2.5, 10.15) * mm, "radius": 0.5 * mm});
            skCircle(sketch, "E68", {"center": v(-2.5, 10.15) * mm, "radius": 0.5 * mm});
            skPoint(sketch, "E69.centerSnap0", {"position": v(8.15, 0) * mm});
            skLineSegment(sketch, "E70.bottom", {"start": v(-8.15, -2.5) * mm, "end": v(-11.15, -2.5) * mm});
            skLineSegment(sketch, "E70.top", {"start": v(-8.15, 2.5) * mm, "end": v(-11.15, 2.5) * mm});
            skLineSegment(sketch, "E70.left", {"start": v(-8.15, -2.5) * mm, "end": v(-8.15, 2.5) * mm});
            skLineSegment(sketch, "E70.right", {"start": v(-11.15, -2.5) * mm, "end": v(-11.15, 2.5) * mm});
            skLineSegment(sketch, "E71.bottom", {"start": v(8.15, -2.5) * mm, "end": v(11.15, -2.5) * mm});
            skLineSegment(sketch, "E71.top", {"start": v(8.15, 2.5) * mm, "end": v(11.15, 2.5) * mm});
            skLineSegment(sketch, "E71.left", {"start": v(8.15, -2.5) * mm, "end": v(8.15, 2.5) * mm});
            skLineSegment(sketch, "E71.right", {"start": v(11.15, -2.5) * mm, "end": v(11.15, 2.5) * mm});
            skLineSegment(sketch, "E72.bottom", {"start": v(-8.15, -2.5) * mm, "end": v(-5.15, -2.5) * mm});
            skLineSegment(sketch, "E72.top", {"start": v(-8.15, 2.5) * mm, "end": v(-5.15, 2.5) * mm});
            skLineSegment(sketch, "E72.right", {"start": v(-5.15, -2.5) * mm, "end": v(-5.15, 2.5) * mm});
            skLineSegment(sketch, "E73.bottom", {"start": v(8.15, -2.5) * mm, "end": v(5.15, -2.5) * mm});
            skLineSegment(sketch, "E73.top", {"start": v(8.15, 2.5) * mm, "end": v(5.15, 2.5) * mm});
            skLineSegment(sketch, "E73.right", {"start": v(5.15, -2.5) * mm, "end": v(5.15, 2.5) * mm});
            skSolve(sketch);
        }
        {
            var Q0;
            {var subQ0=sQuery(id+"F0.wireOp",EDGE,"E6");var subQ1=makeQuery(id+"F7.opExtrude","CAP_EDGE",EDGE,{"disambiguationData":[OSD([subQ0])],"isStart":false});var subQ2=sQuery(id+"F21.wireOp",EDGE,"E67");var subQ3=makeQuery(id+"F21.imprint","INTERSECT",VERTEX,{"derivedFrom":[subQ1,subQ2]});Q0=makeQuery(id+"F21.imprint","IMPRINT",FACE,{"disambiguationData":[TD([[makeQuery(id+"F21.imprint","IMPRINT",EDGE,{"disambiguationData":[TD([[subQ3,1.0]])],"derivedFrom":subQ2}),1.0]])]});}
            var Q1;
            {var subQ1=sQuery(id+"F0.wireOp",EDGE,"E4");var subQ3=sQuery(id+"F21.wireOp",EDGE,"E68");var subQ5=makeQuery(id+"F7.opExtrude","CAP_EDGE",EDGE,{"disambiguationData":[OSD([subQ1])],"isStart":false});var subQ7=makeQuery(id+"F21.imprint","INTERSECT",VERTEX,{"derivedFrom":[subQ5,subQ3]});Q1=makeQuery(id+"F21.imprint","IMPRINT",FACE,{"disambiguationData":[TD([[makeQuery(id+"F21.imprint","IMPRINT",EDGE,{"disambiguationData":[TD([[subQ7,-1.0]])],"derivedFrom":subQ3}),1.0]])]});}
            var Q2;
            {var subQ0=sQuery(id+"F21.wireOp",EDGE,"E71.top");var subQ1=sQuery(id+"F21.wireOp",EDGE,"33bc41b5-04d1-491b-9cc3-e2a9688a8de3");var subQ5=makeQuery(id+"F21.imprint","INTERSECT",VERTEX,{"disambiguationData":[OD(0.0)],"derivedFrom":[subQ1,subQ0]});Q2=makeQuery(id+"F21.imprint","IMPRINT",FACE,{"disambiguationData":[TD([[makeQuery(id+"F21.imprint","IMPRINT",EDGE,{"disambiguationData":[TD([[subQ5,1.0]])],"derivedFrom":subQ1}),1.0]])]});}
            var Q3;
            {var subQ1=sQuery(id+"F21.wireOp",EDGE,"E71.right");Q3=makeQuery(id+"F21.imprint","IMPRINT",FACE,{"disambiguationData":[TD([[makeQuery(id+"F21.imprint","IMPRINT",EDGE,{"derivedFrom":subQ1}),1.0]])]});}
            var Q4;
            {var subQ0=sQuery(id+"F21.wireOp",EDGE,"E70.top");var subQ1=sQuery(id+"F21.wireOp",EDGE,"531c82b6-ca83-49b7-b213-6d50da28229b");var subQ5=makeQuery(id+"F21.imprint","INTERSECT",VERTEX,{"disambiguationData":[OD(0.0)],"derivedFrom":[subQ1,subQ0]});Q4=makeQuery(id+"F21.imprint","IMPRINT",FACE,{"disambiguationData":[TD([[makeQuery(id+"F21.imprint","IMPRINT",EDGE,{"disambiguationData":[TD([[subQ5,-1.0]])],"derivedFrom":subQ1}),1.0]])]});}
            var Q5;
            {var subQ1=sQuery(id+"F21.wireOp",EDGE,"E70.right");Q5=makeQuery(id+"F21.imprint","IMPRINT",FACE,{"disambiguationData":[TD([[makeQuery(id+"F21.imprint","IMPRINT",EDGE,{"derivedFrom":subQ1}),-1.0]])]});}
            var Q6;
            Q6=makeQuery(id+"F3.opExtrude","CAP_FACE",FACE,{"disambiguationData":[OSD([sQuery(id+"F0.wireOp",EDGE,"E0.rect.bottom"),sQuery(id+"F0.wireOp",EDGE,"E0.rect.top"),sQuery(id+"F0.wireOp",EDGE,"E0.rect.left"),sQuery(id+"F0.wireOp",EDGE,"E0.rect.right"),sQuery(id+"F0.wireOp",EDGE,"E1"),sQuery(id+"F0.wireOp",EDGE,"E2"),sQuery(id+"F0.wireOp",EDGE,"E3"),sQuery(id+"F0.wireOp",EDGE,"E4"),sQuery(id+"F0.wireOp",EDGE,"E5"),sQuery(id+"F0.wireOp",EDGE,"E6"),sQuery(id+"F0.wireOp",EDGE,"E7"),sQuery(id+"F0.wireOp",EDGE,"E8"),sQuery(id+"F0.wireOp",EDGE,"E9"),sQuery(id+"F0.wireOp",EDGE,"E10"),sQuery(id+"F0.wireOp",EDGE,"E11"),sQuery(id+"F0.wireOp",EDGE,"E12"),sQuery(id+"F0.wireOp",EDGE,"E13"),sQuery(id+"F0.wireOp",EDGE,"E14"),sQuery(id+"F0.wireOp",EDGE,"E15"),sQuery(id+"F0.wireOp",EDGE,"E16"),sQuery(id+"F0.wireOp",EDGE,"E17.filletArc"),sQuery(id+"F0.wireOp",EDGE,"E28"),sQuery(id+"F0.wireOp",EDGE,"E29"),sQuery(id+"F0.wireOp",EDGE,"E30"),sQuery(id+"F0.wireOp",EDGE,"E31"),sQuery(id+"F0.wireOp",EDGE,"E32"),sQuery(id+"F0.wireOp",EDGE,"E33"),sQuery(id+"F0.wireOp",EDGE,"E34"),sQuery(id+"F0.wireOp",EDGE,"E35"),sQuery(id+"F0.wireOp",EDGE,"E37"),sQuery(id+"F0.wireOp",EDGE,"E39"),sQuery(id+"F2.wireOp",EDGE,"E40.0"),sQuery(id+"F2.wireOp",EDGE,"E41.0"),sQuery(id+"F2.wireOp",EDGE,"E42.0"),sQuery(id+"F2.wireOp",EDGE,"E43.0")])],"isStart":false});
            extrude(context, id + "F22", {"entities" : qUnion([Q0, Q1, Q2, Q3, Q4, Q5]), "operationType" : NewBodyOperationType.REMOVE, "endBound" : BoundingType.UP_TO_SURFACE, "endBoundEntityFace" : qUnion([Q6]), "depth" : 25 * mm});
        }
        {
            var Q0;
            {var subQ1=sQuery(id+"F21.wireOp",EDGE,"E70.right");Q0=makeQuery(id+"F21.imprint","IMPRINT",FACE,{"disambiguationData":[TD([[makeQuery(id+"F21.imprint","IMPRINT",EDGE,{"derivedFrom":subQ1}),-1.0]])]});}
            var Q1;
            {var subQ0=sQuery(id+"F21.wireOp",EDGE,"E70.top");var subQ1=sQuery(id+"F21.wireOp",EDGE,"531c82b6-ca83-49b7-b213-6d50da28229b");var subQ5=makeQuery(id+"F21.imprint","INTERSECT",VERTEX,{"disambiguationData":[OD(0.0)],"derivedFrom":[subQ1,subQ0]});Q1=makeQuery(id+"F21.imprint","IMPRINT",FACE,{"disambiguationData":[TD([[makeQuery(id+"F21.imprint","IMPRINT",EDGE,{"disambiguationData":[TD([[subQ5,-1.0]])],"derivedFrom":subQ1}),1.0]])]});}
            var Q2;
            {var subQ0=sQuery(id+"F21.wireOp",EDGE,"E70.bottom");var subQ1=sQuery(id+"F21.wireOp",EDGE,"ac99823a-828a-4d09-af91-54ec1811b827");var subQ2=makeQuery(id+"F21.imprint","INTERSECT",VERTEX,{"disambiguationData":[OD(0.0)],"derivedFrom":[subQ1,subQ0]});Q2=makeQuery(id+"F21.imprint","IMPRINT",FACE,{"disambiguationData":[TD([[makeQuery(id+"F21.imprint","IMPRINT",EDGE,{"disambiguationData":[TD([[subQ2,1.0]])],"derivedFrom":subQ1}),1.0]])]});}
            var Q3;
            Q3=makeQuery(id+"F21.imprint","IMPRINT",FACE,{"disambiguationData":[TD([[makeQuery(id+"F21.imprint","IMPRINT",EDGE,{"derivedFrom":sQuery(id+"F21.wireOp",EDGE,"E72.bottom")}),1.0]])]});
            var Q4;
            Q4=makeQuery(id+"F21.imprint","IMPRINT",FACE,{"disambiguationData":[TD([[makeQuery(id+"F21.imprint","IMPRINT",EDGE,{"derivedFrom":sQuery(id+"F21.wireOp",EDGE,"E73.bottom")}),-1.0]])]});
            var Q5;
            {var subQ1=sQuery(id+"F21.wireOp",EDGE,"E71.right");Q5=makeQuery(id+"F21.imprint","IMPRINT",FACE,{"disambiguationData":[TD([[makeQuery(id+"F21.imprint","IMPRINT",EDGE,{"derivedFrom":subQ1}),1.0]])]});}
            var Q6;
            {var subQ0=sQuery(id+"F21.wireOp",EDGE,"E71.top");var subQ1=sQuery(id+"F21.wireOp",EDGE,"33bc41b5-04d1-491b-9cc3-e2a9688a8de3");var subQ5=makeQuery(id+"F21.imprint","INTERSECT",VERTEX,{"disambiguationData":[OD(0.0)],"derivedFrom":[subQ1,subQ0]});Q6=makeQuery(id+"F21.imprint","IMPRINT",FACE,{"disambiguationData":[TD([[makeQuery(id+"F21.imprint","IMPRINT",EDGE,{"disambiguationData":[TD([[subQ5,1.0]])],"derivedFrom":subQ1}),1.0]])]});}
            var Q7;
            {var subQ0=sQuery(id+"F21.wireOp",EDGE,"E71.bottom");var subQ1=sQuery(id+"F21.wireOp",EDGE,"98ab61b8-06a1-4cc8-8eb2-811207c01617");var subQ5=makeQuery(id+"F21.imprint","INTERSECT",VERTEX,{"disambiguationData":[OD(0.0)],"derivedFrom":[subQ1,subQ0]});Q7=makeQuery(id+"F21.imprint","IMPRINT",FACE,{"disambiguationData":[TD([[makeQuery(id+"F21.imprint","IMPRINT",EDGE,{"disambiguationData":[TD([[subQ5,-1.0]])],"derivedFrom":subQ1}),1.0]])]});}
            extrude(context, id + "F23", {"entities" : qUnion([Q0, Q1, Q2, Q3, Q4, Q5, Q6, Q7]), "operationType" : NewBodyOperationType.REMOVE, "oppositeDirection" : true, "depth" : 25 * mm});
        }
        {
            var Q0;
            {var subQ0=sQuery(id+"F0.wireOp",EDGE,"E0.rect.bottom");var subQ1=sQuery(id+"F0.wireOp",EDGE,"E0.rect.top");var subQ2=sQuery(id+"F0.wireOp",EDGE,"E0.rect.left");var subQ3=sQuery(id+"F0.wireOp",EDGE,"E0.rect.right");var subQ4=sQuery(id+"F0.wireOp",EDGE,"E1");var subQ5=sQuery(id+"F0.wireOp",EDGE,"E2");var subQ6=sQuery(id+"F0.wireOp",EDGE,"E3");var subQ7=sQuery(id+"F0.wireOp",EDGE,"E4");var subQ8=sQuery(id+"F0.wireOp",EDGE,"E5");var subQ9=sQuery(id+"F0.wireOp",EDGE,"E6");var subQ10=sQuery(id+"F0.wireOp",EDGE,"E7");var subQ11=sQuery(id+"F0.wireOp",EDGE,"E8");var subQ12=sQuery(id+"F0.wireOp",EDGE,"E9");Q0=makeQuery(id+"F23.boolean.opBoolean","INTERSECT",EDGE,{"derivedFrom":[makeQuery(id+"F7.boolean.opBoolean","MERGE",FACE,{"derivedFrom":[makeQuery(id+"F1.opExtrude","CAP_FACE",FACE,{"disambiguationData":[OSD([subQ0,subQ1,subQ2,subQ3,subQ4,subQ5,subQ6,subQ7,subQ8,subQ9,subQ10,subQ11,subQ12,sQuery(id+"F0.wireOp",EDGE,"E10"),sQuery(id+"F0.wireOp",EDGE,"E11"),sQuery(id+"F0.wireOp",EDGE,"E12"),sQuery(id+"F0.wireOp",EDGE,"E13"),sQuery(id+"F0.wireOp",EDGE,"E14"),sQuery(id+"F0.wireOp",EDGE,"E15"),sQuery(id+"F0.wireOp",EDGE,"E16"),sQuery(id+"F0.wireOp",EDGE,"E17.filletArc"),sQuery(id+"F0.wireOp",EDGE,"E24"),sQuery(id+"F0.wireOp",EDGE,"E25"),sQuery(id+"F0.wireOp",EDGE,"E26"),sQuery(id+"F0.wireOp",EDGE,"E27"),sQuery(id+"F0.wireOp",EDGE,"E28"),sQuery(id+"F0.wireOp",EDGE,"E29"),sQuery(id+"F0.wireOp",EDGE,"E30"),sQuery(id+"F0.wireOp",EDGE,"E31"),sQuery(id+"F0.wireOp",EDGE,"E32"),sQuery(id+"F0.wireOp",EDGE,"E33"),sQuery(id+"F0.wireOp",EDGE,"E34"),sQuery(id+"F0.wireOp",EDGE,"E35"),sQuery(id+"F0.wireOp",EDGE,"E37"),sQuery(id+"F0.wireOp",EDGE,"E39")])],"isStart":true}),makeQuery(id+"F7.opExtrude","CAP_FACE",FACE,{"disambiguationData":[OSD([subQ0,subQ1,subQ2,subQ3,subQ4,subQ5,subQ6,subQ7,subQ8,subQ9,subQ10,subQ11,subQ12])],"isStart":true})]}),makeQuery(id+"F23.opExtrude","SWEPT_FACE",FACE,{"disambiguationData":[OSD([sQuery(id+"F21.wireOp",EDGE,"E70.right")])]})]});}
            var Q1;
            {var subQ0=sQuery(id+"F0.wireOp",EDGE,"E0.rect.bottom");var subQ1=sQuery(id+"F0.wireOp",EDGE,"E0.rect.top");var subQ2=sQuery(id+"F0.wireOp",EDGE,"E0.rect.left");var subQ3=sQuery(id+"F0.wireOp",EDGE,"E0.rect.right");var subQ4=sQuery(id+"F0.wireOp",EDGE,"E1");var subQ5=sQuery(id+"F0.wireOp",EDGE,"E2");var subQ6=sQuery(id+"F0.wireOp",EDGE,"E3");var subQ7=sQuery(id+"F0.wireOp",EDGE,"E4");var subQ8=sQuery(id+"F0.wireOp",EDGE,"E5");var subQ9=sQuery(id+"F0.wireOp",EDGE,"E6");var subQ10=sQuery(id+"F0.wireOp",EDGE,"E7");var subQ11=sQuery(id+"F0.wireOp",EDGE,"E8");var subQ12=sQuery(id+"F0.wireOp",EDGE,"E9");Q1=makeQuery(id+"F23.boolean.opBoolean","INTERSECT",EDGE,{"derivedFrom":[makeQuery(id+"F7.boolean.opBoolean","MERGE",FACE,{"derivedFrom":[makeQuery(id+"F1.opExtrude","CAP_FACE",FACE,{"disambiguationData":[OSD([subQ0,subQ1,subQ2,subQ3,subQ4,subQ5,subQ6,subQ7,subQ8,subQ9,subQ10,subQ11,subQ12,sQuery(id+"F0.wireOp",EDGE,"E10"),sQuery(id+"F0.wireOp",EDGE,"E11"),sQuery(id+"F0.wireOp",EDGE,"E12"),sQuery(id+"F0.wireOp",EDGE,"E13"),sQuery(id+"F0.wireOp",EDGE,"E14"),sQuery(id+"F0.wireOp",EDGE,"E15"),sQuery(id+"F0.wireOp",EDGE,"E16"),sQuery(id+"F0.wireOp",EDGE,"E17.filletArc"),sQuery(id+"F0.wireOp",EDGE,"E24"),sQuery(id+"F0.wireOp",EDGE,"E25"),sQuery(id+"F0.wireOp",EDGE,"E26"),sQuery(id+"F0.wireOp",EDGE,"E27"),sQuery(id+"F0.wireOp",EDGE,"E28"),sQuery(id+"F0.wireOp",EDGE,"E29"),sQuery(id+"F0.wireOp",EDGE,"E30"),sQuery(id+"F0.wireOp",EDGE,"E31"),sQuery(id+"F0.wireOp",EDGE,"E32"),sQuery(id+"F0.wireOp",EDGE,"E33"),sQuery(id+"F0.wireOp",EDGE,"E34"),sQuery(id+"F0.wireOp",EDGE,"E35"),sQuery(id+"F0.wireOp",EDGE,"E37"),sQuery(id+"F0.wireOp",EDGE,"E39")])],"isStart":true}),makeQuery(id+"F7.opExtrude","CAP_FACE",FACE,{"disambiguationData":[OSD([subQ0,subQ1,subQ2,subQ3,subQ4,subQ5,subQ6,subQ7,subQ8,subQ9,subQ10,subQ11,subQ12])],"isStart":true})]}),makeQuery(id+"F23.opExtrude","SWEPT_FACE",FACE,{"disambiguationData":[OSD([sQuery(id+"F21.wireOp",EDGE,"E70.bottom"),sQuery(id+"F21.wireOp",EDGE,"E72.bottom")])]})]});}
            var Q2;
            {var subQ0=sQuery(id+"F0.wireOp",EDGE,"E0.rect.bottom");var subQ1=sQuery(id+"F0.wireOp",EDGE,"E0.rect.top");var subQ2=sQuery(id+"F0.wireOp",EDGE,"E0.rect.left");var subQ3=sQuery(id+"F0.wireOp",EDGE,"E0.rect.right");var subQ4=sQuery(id+"F0.wireOp",EDGE,"E1");var subQ5=sQuery(id+"F0.wireOp",EDGE,"E2");var subQ6=sQuery(id+"F0.wireOp",EDGE,"E3");var subQ7=sQuery(id+"F0.wireOp",EDGE,"E4");var subQ8=sQuery(id+"F0.wireOp",EDGE,"E5");var subQ9=sQuery(id+"F0.wireOp",EDGE,"E6");var subQ10=sQuery(id+"F0.wireOp",EDGE,"E7");var subQ11=sQuery(id+"F0.wireOp",EDGE,"E8");var subQ12=sQuery(id+"F0.wireOp",EDGE,"E9");Q2=makeQuery(id+"F23.boolean.opBoolean","INTERSECT",EDGE,{"derivedFrom":[makeQuery(id+"F7.boolean.opBoolean","MERGE",FACE,{"derivedFrom":[makeQuery(id+"F1.opExtrude","CAP_FACE",FACE,{"disambiguationData":[OSD([subQ0,subQ1,subQ2,subQ3,subQ4,subQ5,subQ6,subQ7,subQ8,subQ9,subQ10,subQ11,subQ12,sQuery(id+"F0.wireOp",EDGE,"E10"),sQuery(id+"F0.wireOp",EDGE,"E11"),sQuery(id+"F0.wireOp",EDGE,"E12"),sQuery(id+"F0.wireOp",EDGE,"E13"),sQuery(id+"F0.wireOp",EDGE,"E14"),sQuery(id+"F0.wireOp",EDGE,"E15"),sQuery(id+"F0.wireOp",EDGE,"E16"),sQuery(id+"F0.wireOp",EDGE,"E17.filletArc"),sQuery(id+"F0.wireOp",EDGE,"E24"),sQuery(id+"F0.wireOp",EDGE,"E25"),sQuery(id+"F0.wireOp",EDGE,"E26"),sQuery(id+"F0.wireOp",EDGE,"E27"),sQuery(id+"F0.wireOp",EDGE,"E28"),sQuery(id+"F0.wireOp",EDGE,"E29"),sQuery(id+"F0.wireOp",EDGE,"E30"),sQuery(id+"F0.wireOp",EDGE,"E31"),sQuery(id+"F0.wireOp",EDGE,"E32"),sQuery(id+"F0.wireOp",EDGE,"E33"),sQuery(id+"F0.wireOp",EDGE,"E34"),sQuery(id+"F0.wireOp",EDGE,"E35"),sQuery(id+"F0.wireOp",EDGE,"E37"),sQuery(id+"F0.wireOp",EDGE,"E39")])],"isStart":true}),makeQuery(id+"F7.opExtrude","CAP_FACE",FACE,{"disambiguationData":[OSD([subQ0,subQ1,subQ2,subQ3,subQ4,subQ5,subQ6,subQ7,subQ8,subQ9,subQ10,subQ11,subQ12])],"isStart":true})]}),makeQuery(id+"F23.opExtrude","SWEPT_FACE",FACE,{"disambiguationData":[OSD([sQuery(id+"F21.wireOp",EDGE,"E72.right")])]})]});}
            var Q3;
            {var subQ0=sQuery(id+"F0.wireOp",EDGE,"E0.rect.bottom");var subQ1=sQuery(id+"F0.wireOp",EDGE,"E0.rect.top");var subQ2=sQuery(id+"F0.wireOp",EDGE,"E0.rect.left");var subQ3=sQuery(id+"F0.wireOp",EDGE,"E0.rect.right");var subQ4=sQuery(id+"F0.wireOp",EDGE,"E1");var subQ5=sQuery(id+"F0.wireOp",EDGE,"E2");var subQ6=sQuery(id+"F0.wireOp",EDGE,"E3");var subQ7=sQuery(id+"F0.wireOp",EDGE,"E4");var subQ8=sQuery(id+"F0.wireOp",EDGE,"E5");var subQ9=sQuery(id+"F0.wireOp",EDGE,"E6");var subQ10=sQuery(id+"F0.wireOp",EDGE,"E7");var subQ11=sQuery(id+"F0.wireOp",EDGE,"E8");var subQ12=sQuery(id+"F0.wireOp",EDGE,"E9");Q3=makeQuery(id+"F23.boolean.opBoolean","INTERSECT",EDGE,{"derivedFrom":[makeQuery(id+"F7.boolean.opBoolean","MERGE",FACE,{"derivedFrom":[makeQuery(id+"F1.opExtrude","CAP_FACE",FACE,{"disambiguationData":[OSD([subQ0,subQ1,subQ2,subQ3,subQ4,subQ5,subQ6,subQ7,subQ8,subQ9,subQ10,subQ11,subQ12,sQuery(id+"F0.wireOp",EDGE,"E10"),sQuery(id+"F0.wireOp",EDGE,"E11"),sQuery(id+"F0.wireOp",EDGE,"E12"),sQuery(id+"F0.wireOp",EDGE,"E13"),sQuery(id+"F0.wireOp",EDGE,"E14"),sQuery(id+"F0.wireOp",EDGE,"E15"),sQuery(id+"F0.wireOp",EDGE,"E16"),sQuery(id+"F0.wireOp",EDGE,"E17.filletArc"),sQuery(id+"F0.wireOp",EDGE,"E24"),sQuery(id+"F0.wireOp",EDGE,"E25"),sQuery(id+"F0.wireOp",EDGE,"E26"),sQuery(id+"F0.wireOp",EDGE,"E27"),sQuery(id+"F0.wireOp",EDGE,"E28"),sQuery(id+"F0.wireOp",EDGE,"E29"),sQuery(id+"F0.wireOp",EDGE,"E30"),sQuery(id+"F0.wireOp",EDGE,"E31"),sQuery(id+"F0.wireOp",EDGE,"E32"),sQuery(id+"F0.wireOp",EDGE,"E33"),sQuery(id+"F0.wireOp",EDGE,"E34"),sQuery(id+"F0.wireOp",EDGE,"E35"),sQuery(id+"F0.wireOp",EDGE,"E37"),sQuery(id+"F0.wireOp",EDGE,"E39")])],"isStart":true}),makeQuery(id+"F7.opExtrude","CAP_FACE",FACE,{"disambiguationData":[OSD([subQ0,subQ1,subQ2,subQ3,subQ4,subQ5,subQ6,subQ7,subQ8,subQ9,subQ10,subQ11,subQ12])],"isStart":true})]}),makeQuery(id+"F23.opExtrude","SWEPT_FACE",FACE,{"disambiguationData":[OSD([sQuery(id+"F21.wireOp",EDGE,"E70.top"),sQuery(id+"F21.wireOp",EDGE,"E72.top")])]})]});}
            var Q4;
            {var subQ0=sQuery(id+"F0.wireOp",EDGE,"E0.rect.bottom");var subQ1=sQuery(id+"F0.wireOp",EDGE,"E0.rect.top");var subQ2=sQuery(id+"F0.wireOp",EDGE,"E0.rect.left");var subQ3=sQuery(id+"F0.wireOp",EDGE,"E0.rect.right");var subQ4=sQuery(id+"F0.wireOp",EDGE,"E1");var subQ5=sQuery(id+"F0.wireOp",EDGE,"E2");var subQ6=sQuery(id+"F0.wireOp",EDGE,"E3");var subQ7=sQuery(id+"F0.wireOp",EDGE,"E4");var subQ8=sQuery(id+"F0.wireOp",EDGE,"E5");var subQ9=sQuery(id+"F0.wireOp",EDGE,"E6");var subQ10=sQuery(id+"F0.wireOp",EDGE,"E7");var subQ11=sQuery(id+"F0.wireOp",EDGE,"E8");var subQ12=sQuery(id+"F0.wireOp",EDGE,"E9");Q4=makeQuery(id+"F23.boolean.opBoolean","INTERSECT",EDGE,{"derivedFrom":[makeQuery(id+"F7.boolean.opBoolean","MERGE",FACE,{"derivedFrom":[makeQuery(id+"F1.opExtrude","CAP_FACE",FACE,{"disambiguationData":[OSD([subQ0,subQ1,subQ2,subQ3,subQ4,subQ5,subQ6,subQ7,subQ8,subQ9,subQ10,subQ11,subQ12,sQuery(id+"F0.wireOp",EDGE,"E10"),sQuery(id+"F0.wireOp",EDGE,"E11"),sQuery(id+"F0.wireOp",EDGE,"E12"),sQuery(id+"F0.wireOp",EDGE,"E13"),sQuery(id+"F0.wireOp",EDGE,"E14"),sQuery(id+"F0.wireOp",EDGE,"E15"),sQuery(id+"F0.wireOp",EDGE,"E16"),sQuery(id+"F0.wireOp",EDGE,"E17.filletArc"),sQuery(id+"F0.wireOp",EDGE,"E24"),sQuery(id+"F0.wireOp",EDGE,"E25"),sQuery(id+"F0.wireOp",EDGE,"E26"),sQuery(id+"F0.wireOp",EDGE,"E27"),sQuery(id+"F0.wireOp",EDGE,"E28"),sQuery(id+"F0.wireOp",EDGE,"E29"),sQuery(id+"F0.wireOp",EDGE,"E30"),sQuery(id+"F0.wireOp",EDGE,"E31"),sQuery(id+"F0.wireOp",EDGE,"E32"),sQuery(id+"F0.wireOp",EDGE,"E33"),sQuery(id+"F0.wireOp",EDGE,"E34"),sQuery(id+"F0.wireOp",EDGE,"E35"),sQuery(id+"F0.wireOp",EDGE,"E37"),sQuery(id+"F0.wireOp",EDGE,"E39")])],"isStart":true}),makeQuery(id+"F7.opExtrude","CAP_FACE",FACE,{"disambiguationData":[OSD([subQ0,subQ1,subQ2,subQ3,subQ4,subQ5,subQ6,subQ7,subQ8,subQ9,subQ10,subQ11,subQ12])],"isStart":true})]}),makeQuery(id+"F23.opExtrude","SWEPT_FACE",FACE,{"disambiguationData":[OSD([sQuery(id+"F21.wireOp",EDGE,"E73.right")])]})]});}
            var Q5;
            {var subQ0=sQuery(id+"F0.wireOp",EDGE,"E0.rect.bottom");var subQ1=sQuery(id+"F0.wireOp",EDGE,"E0.rect.top");var subQ2=sQuery(id+"F0.wireOp",EDGE,"E0.rect.left");var subQ3=sQuery(id+"F0.wireOp",EDGE,"E0.rect.right");var subQ4=sQuery(id+"F0.wireOp",EDGE,"E1");var subQ5=sQuery(id+"F0.wireOp",EDGE,"E2");var subQ6=sQuery(id+"F0.wireOp",EDGE,"E3");var subQ7=sQuery(id+"F0.wireOp",EDGE,"E4");var subQ8=sQuery(id+"F0.wireOp",EDGE,"E5");var subQ9=sQuery(id+"F0.wireOp",EDGE,"E6");var subQ10=sQuery(id+"F0.wireOp",EDGE,"E7");var subQ11=sQuery(id+"F0.wireOp",EDGE,"E8");var subQ12=sQuery(id+"F0.wireOp",EDGE,"E9");Q5=makeQuery(id+"F23.boolean.opBoolean","INTERSECT",EDGE,{"derivedFrom":[makeQuery(id+"F7.boolean.opBoolean","MERGE",FACE,{"derivedFrom":[makeQuery(id+"F1.opExtrude","CAP_FACE",FACE,{"disambiguationData":[OSD([subQ0,subQ1,subQ2,subQ3,subQ4,subQ5,subQ6,subQ7,subQ8,subQ9,subQ10,subQ11,subQ12,sQuery(id+"F0.wireOp",EDGE,"E10"),sQuery(id+"F0.wireOp",EDGE,"E11"),sQuery(id+"F0.wireOp",EDGE,"E12"),sQuery(id+"F0.wireOp",EDGE,"E13"),sQuery(id+"F0.wireOp",EDGE,"E14"),sQuery(id+"F0.wireOp",EDGE,"E15"),sQuery(id+"F0.wireOp",EDGE,"E16"),sQuery(id+"F0.wireOp",EDGE,"E17.filletArc"),sQuery(id+"F0.wireOp",EDGE,"E24"),sQuery(id+"F0.wireOp",EDGE,"E25"),sQuery(id+"F0.wireOp",EDGE,"E26"),sQuery(id+"F0.wireOp",EDGE,"E27"),sQuery(id+"F0.wireOp",EDGE,"E28"),sQuery(id+"F0.wireOp",EDGE,"E29"),sQuery(id+"F0.wireOp",EDGE,"E30"),sQuery(id+"F0.wireOp",EDGE,"E31"),sQuery(id+"F0.wireOp",EDGE,"E32"),sQuery(id+"F0.wireOp",EDGE,"E33"),sQuery(id+"F0.wireOp",EDGE,"E34"),sQuery(id+"F0.wireOp",EDGE,"E35"),sQuery(id+"F0.wireOp",EDGE,"E37"),sQuery(id+"F0.wireOp",EDGE,"E39")])],"isStart":true}),makeQuery(id+"F7.opExtrude","CAP_FACE",FACE,{"disambiguationData":[OSD([subQ0,subQ1,subQ2,subQ3,subQ4,subQ5,subQ6,subQ7,subQ8,subQ9,subQ10,subQ11,subQ12])],"isStart":true})]}),makeQuery(id+"F23.opExtrude","SWEPT_FACE",FACE,{"disambiguationData":[OSD([sQuery(id+"F21.wireOp",EDGE,"E71.bottom"),sQuery(id+"F21.wireOp",EDGE,"E73.bottom")])]})]});}
            var Q6;
            {var subQ0=sQuery(id+"F0.wireOp",EDGE,"E0.rect.bottom");var subQ1=sQuery(id+"F0.wireOp",EDGE,"E0.rect.top");var subQ2=sQuery(id+"F0.wireOp",EDGE,"E0.rect.left");var subQ3=sQuery(id+"F0.wireOp",EDGE,"E0.rect.right");var subQ4=sQuery(id+"F0.wireOp",EDGE,"E1");var subQ5=sQuery(id+"F0.wireOp",EDGE,"E2");var subQ6=sQuery(id+"F0.wireOp",EDGE,"E3");var subQ7=sQuery(id+"F0.wireOp",EDGE,"E4");var subQ8=sQuery(id+"F0.wireOp",EDGE,"E5");var subQ9=sQuery(id+"F0.wireOp",EDGE,"E6");var subQ10=sQuery(id+"F0.wireOp",EDGE,"E7");var subQ11=sQuery(id+"F0.wireOp",EDGE,"E8");var subQ12=sQuery(id+"F0.wireOp",EDGE,"E9");Q6=makeQuery(id+"F23.boolean.opBoolean","INTERSECT",EDGE,{"derivedFrom":[makeQuery(id+"F7.boolean.opBoolean","MERGE",FACE,{"derivedFrom":[makeQuery(id+"F1.opExtrude","CAP_FACE",FACE,{"disambiguationData":[OSD([subQ0,subQ1,subQ2,subQ3,subQ4,subQ5,subQ6,subQ7,subQ8,subQ9,subQ10,subQ11,subQ12,sQuery(id+"F0.wireOp",EDGE,"E10"),sQuery(id+"F0.wireOp",EDGE,"E11"),sQuery(id+"F0.wireOp",EDGE,"E12"),sQuery(id+"F0.wireOp",EDGE,"E13"),sQuery(id+"F0.wireOp",EDGE,"E14"),sQuery(id+"F0.wireOp",EDGE,"E15"),sQuery(id+"F0.wireOp",EDGE,"E16"),sQuery(id+"F0.wireOp",EDGE,"E17.filletArc"),sQuery(id+"F0.wireOp",EDGE,"E24"),sQuery(id+"F0.wireOp",EDGE,"E25"),sQuery(id+"F0.wireOp",EDGE,"E26"),sQuery(id+"F0.wireOp",EDGE,"E27"),sQuery(id+"F0.wireOp",EDGE,"E28"),sQuery(id+"F0.wireOp",EDGE,"E29"),sQuery(id+"F0.wireOp",EDGE,"E30"),sQuery(id+"F0.wireOp",EDGE,"E31"),sQuery(id+"F0.wireOp",EDGE,"E32"),sQuery(id+"F0.wireOp",EDGE,"E33"),sQuery(id+"F0.wireOp",EDGE,"E34"),sQuery(id+"F0.wireOp",EDGE,"E35"),sQuery(id+"F0.wireOp",EDGE,"E37"),sQuery(id+"F0.wireOp",EDGE,"E39")])],"isStart":true}),makeQuery(id+"F7.opExtrude","CAP_FACE",FACE,{"disambiguationData":[OSD([subQ0,subQ1,subQ2,subQ3,subQ4,subQ5,subQ6,subQ7,subQ8,subQ9,subQ10,subQ11,subQ12])],"isStart":true})]}),makeQuery(id+"F23.opExtrude","SWEPT_FACE",FACE,{"disambiguationData":[OSD([sQuery(id+"F21.wireOp",EDGE,"E71.right")])]})]});}
            var Q7;
            {var subQ0=sQuery(id+"F0.wireOp",EDGE,"E0.rect.bottom");var subQ1=sQuery(id+"F0.wireOp",EDGE,"E0.rect.top");var subQ2=sQuery(id+"F0.wireOp",EDGE,"E0.rect.left");var subQ3=sQuery(id+"F0.wireOp",EDGE,"E0.rect.right");var subQ4=sQuery(id+"F0.wireOp",EDGE,"E1");var subQ5=sQuery(id+"F0.wireOp",EDGE,"E2");var subQ6=sQuery(id+"F0.wireOp",EDGE,"E3");var subQ7=sQuery(id+"F0.wireOp",EDGE,"E4");var subQ8=sQuery(id+"F0.wireOp",EDGE,"E5");var subQ9=sQuery(id+"F0.wireOp",EDGE,"E6");var subQ10=sQuery(id+"F0.wireOp",EDGE,"E7");var subQ11=sQuery(id+"F0.wireOp",EDGE,"E8");var subQ12=sQuery(id+"F0.wireOp",EDGE,"E9");Q7=makeQuery(id+"F23.boolean.opBoolean","INTERSECT",EDGE,{"derivedFrom":[makeQuery(id+"F7.boolean.opBoolean","MERGE",FACE,{"derivedFrom":[makeQuery(id+"F1.opExtrude","CAP_FACE",FACE,{"disambiguationData":[OSD([subQ0,subQ1,subQ2,subQ3,subQ4,subQ5,subQ6,subQ7,subQ8,subQ9,subQ10,subQ11,subQ12,sQuery(id+"F0.wireOp",EDGE,"E10"),sQuery(id+"F0.wireOp",EDGE,"E11"),sQuery(id+"F0.wireOp",EDGE,"E12"),sQuery(id+"F0.wireOp",EDGE,"E13"),sQuery(id+"F0.wireOp",EDGE,"E14"),sQuery(id+"F0.wireOp",EDGE,"E15"),sQuery(id+"F0.wireOp",EDGE,"E16"),sQuery(id+"F0.wireOp",EDGE,"E17.filletArc"),sQuery(id+"F0.wireOp",EDGE,"E24"),sQuery(id+"F0.wireOp",EDGE,"E25"),sQuery(id+"F0.wireOp",EDGE,"E26"),sQuery(id+"F0.wireOp",EDGE,"E27"),sQuery(id+"F0.wireOp",EDGE,"E28"),sQuery(id+"F0.wireOp",EDGE,"E29"),sQuery(id+"F0.wireOp",EDGE,"E30"),sQuery(id+"F0.wireOp",EDGE,"E31"),sQuery(id+"F0.wireOp",EDGE,"E32"),sQuery(id+"F0.wireOp",EDGE,"E33"),sQuery(id+"F0.wireOp",EDGE,"E34"),sQuery(id+"F0.wireOp",EDGE,"E35"),sQuery(id+"F0.wireOp",EDGE,"E37"),sQuery(id+"F0.wireOp",EDGE,"E39")])],"isStart":true}),makeQuery(id+"F7.opExtrude","CAP_FACE",FACE,{"disambiguationData":[OSD([subQ0,subQ1,subQ2,subQ3,subQ4,subQ5,subQ6,subQ7,subQ8,subQ9,subQ10,subQ11,subQ12])],"isStart":true})]}),makeQuery(id+"F23.opExtrude","SWEPT_FACE",FACE,{"disambiguationData":[OSD([sQuery(id+"F21.wireOp",EDGE,"E71.top"),sQuery(id+"F21.wireOp",EDGE,"E73.top")])]})]});}
            chamfer(context, id + "F24", {"entities" : qUnion([Q0, Q1, Q2, Q3, Q4, Q5, Q6, Q7]), "width" : 0.5 * mm, "tangentPropagation" : true});
        }
        {
            var Q0;
            {var subQ0=sQuery(id+"F0.wireOp",EDGE,"E5");var subQ1=sQuery(id+"F0.wireOp",EDGE,"E6");Q0=makeQuery(id+"F3.boolean.opBoolean","MERGE",EDGE,{"derivedFrom":[makeQuery(id+"F1.opExtrude","SWEPT_EDGE",EDGE,{"disambiguationData":[OSD([subQ0,subQ1])]}),makeQuery(id+"F3.opExtrude","SWEPT_EDGE",EDGE,{"disambiguationData":[OSD([subQ0,subQ1])]})]});}
            var Q1;
            {var subQ0=sQuery(id+"F0.wireOp",EDGE,"E4");var subQ1=sQuery(id+"F0.wireOp",EDGE,"E5");Q1=makeQuery(id+"F3.boolean.opBoolean","MERGE",EDGE,{"derivedFrom":[makeQuery(id+"F1.opExtrude","SWEPT_EDGE",EDGE,{"disambiguationData":[OSD([subQ0,subQ1])]}),makeQuery(id+"F3.opExtrude","SWEPT_EDGE",EDGE,{"disambiguationData":[OSD([subQ0,subQ1])]})]});}
            var Q2;
            Q2=makeQuery(id+"F22.boolean.opBoolean","COPY",EDGE,{"derivedFrom":makeQuery(id+"F22.opExtrude","SWEPT_EDGE",EDGE,{"disambiguationData":[OSD([sQuery(id+"F0.wireOp",EDGE,"E4"),sQuery(id+"F21.wireOp",EDGE,"E68")])]})});
            var Q3;
            Q3=makeQuery(id+"F22.boolean.opBoolean","COPY",EDGE,{"derivedFrom":makeQuery(id+"F22.opExtrude","SWEPT_EDGE",EDGE,{"disambiguationData":[OSD([sQuery(id+"F0.wireOp",EDGE,"E6"),sQuery(id+"F21.wireOp",EDGE,"E67")])]})});
            var Q4;
            Q4=makeQuery(id+"F22.boolean.opBoolean","COPY",EDGE,{"derivedFrom":makeQuery(id+"F22.opExtrude","SWEPT_EDGE",EDGE,{"disambiguationData":[OSD([sQuery(id+"F0.wireOp",EDGE,"E0.rect.top"),sQuery(id+"F21.wireOp",EDGE,"E67")])]})});
            var Q5;
            Q5=makeQuery(id+"F22.boolean.opBoolean","COPY",EDGE,{"derivedFrom":makeQuery(id+"F22.opExtrude","SWEPT_EDGE",EDGE,{"disambiguationData":[OSD([sQuery(id+"F0.wireOp",EDGE,"E0.rect.top"),sQuery(id+"F21.wireOp",EDGE,"E68")])]})});
            var Q6;
            {var subQ0=sQuery(id+"F0.wireOp",EDGE,"E0.rect.left");var subQ1=sQuery(id+"F0.wireOp",EDGE,"E7");Q6=makeQuery(id+"F3.boolean.opBoolean","MERGE",EDGE,{"derivedFrom":[makeQuery(id+"F1.opExtrude","SWEPT_EDGE",EDGE,{"disambiguationData":[OSD([subQ0,subQ1])]}),makeQuery(id+"F3.opExtrude","SWEPT_EDGE",EDGE,{"disambiguationData":[OSD([subQ0,subQ1])]})]});}
            var Q7;
            {var subQ0=sQuery(id+"F0.wireOp",EDGE,"E0.rect.left");var subQ1=sQuery(id+"F0.wireOp",EDGE,"E9");Q7=makeQuery(id+"F3.boolean.opBoolean","MERGE",EDGE,{"derivedFrom":[makeQuery(id+"F1.opExtrude","SWEPT_EDGE",EDGE,{"disambiguationData":[OSD([subQ0,subQ1])]}),makeQuery(id+"F3.opExtrude","SWEPT_EDGE",EDGE,{"disambiguationData":[OSD([subQ0,subQ1])]})]});}
            var Q8;
            {var subQ0=sQuery(id+"F0.wireOp",EDGE,"E0.rect.right");var subQ1=sQuery(id+"F0.wireOp",EDGE,"E3");Q8=makeQuery(id+"F3.boolean.opBoolean","MERGE",EDGE,{"derivedFrom":[makeQuery(id+"F1.opExtrude","SWEPT_EDGE",EDGE,{"disambiguationData":[OSD([subQ0,subQ1])]}),makeQuery(id+"F3.opExtrude","SWEPT_EDGE",EDGE,{"disambiguationData":[OSD([subQ0,subQ1])]})]});}
            var Q9;
            {var subQ0=sQuery(id+"F0.wireOp",EDGE,"E0.rect.right");var subQ1=sQuery(id+"F0.wireOp",EDGE,"E1");Q9=makeQuery(id+"F3.boolean.opBoolean","MERGE",EDGE,{"derivedFrom":[makeQuery(id+"F1.opExtrude","SWEPT_EDGE",EDGE,{"disambiguationData":[OSD([subQ0,subQ1])]}),makeQuery(id+"F3.opExtrude","SWEPT_EDGE",EDGE,{"disambiguationData":[OSD([subQ0,subQ1])]})]});}
            fillet(context, id + "F25", {"entities" : qUnion([Q0, Q1, Q2, Q3, Q4, Q5, Q6, Q7, Q8, Q9]), "radius" : 0.5 * mm, "tangentPropagation" : true, "allowEdgeOverflow" : false});
        }
    });
